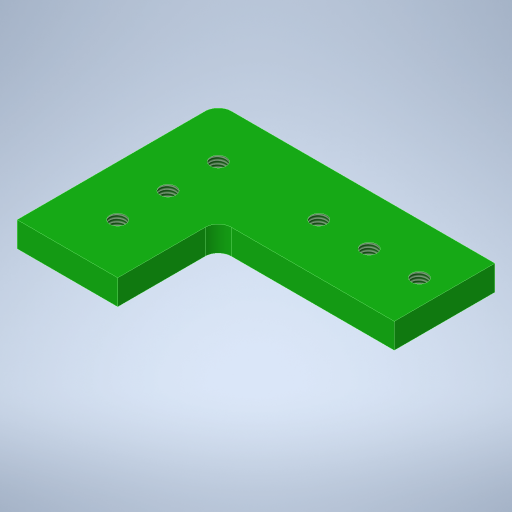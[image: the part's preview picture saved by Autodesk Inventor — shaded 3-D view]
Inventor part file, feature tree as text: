
AUTODESK INVENTOR PART (.ipt)
format: ipt  version: 2023.4 (Build 274418000, 418)  size: 256,000 bytes
history: native  units: in
note: dims shown in document units (in); Inventor stores cm internally (conversion verified against a paired STEP export)
features: sketch x3, extrude x2, hole x1, fillet x1
ambient origin geometry x8: Origin, YZ Plane, XZ Plane, XY Plane, X Axis, Y Axis, Z Axis, Center Point
bodies: Solid1 (feature_tree)
feature tree (7):
  extrude  "Extrusion1"  Depth=2.0in
  extrude  "Extrusion2"  Depth=1.0in
  hole  "Hole2"  [1 undecoded]
  fillet  "Fillet1"  Radius=0.5in
  sketch  "Sketch1"  dims[d0=1.0in d1=2.0in]
  sketch  "Sketch3"  dims[d2=0.25in d3=0.0in d14=1.0in]
  sketch  "Sketch4"  dims[d15=1.75in d16=0.0in d17=0.5in d18=0.5in d19=0.5in d20=1.0in d21=0.5in d22=0.5in d23=0.156in d24=0.38in d25=0.375in d26=0.25in d27=0.5635in d28=1.0in d29=0.8108in d30=0.13in]
note: 1 required parameter value undecoded (feature->parameter linkage not recoverable at this tier; creation-order binding heuristic only, values carry confidence <= 0.55)
